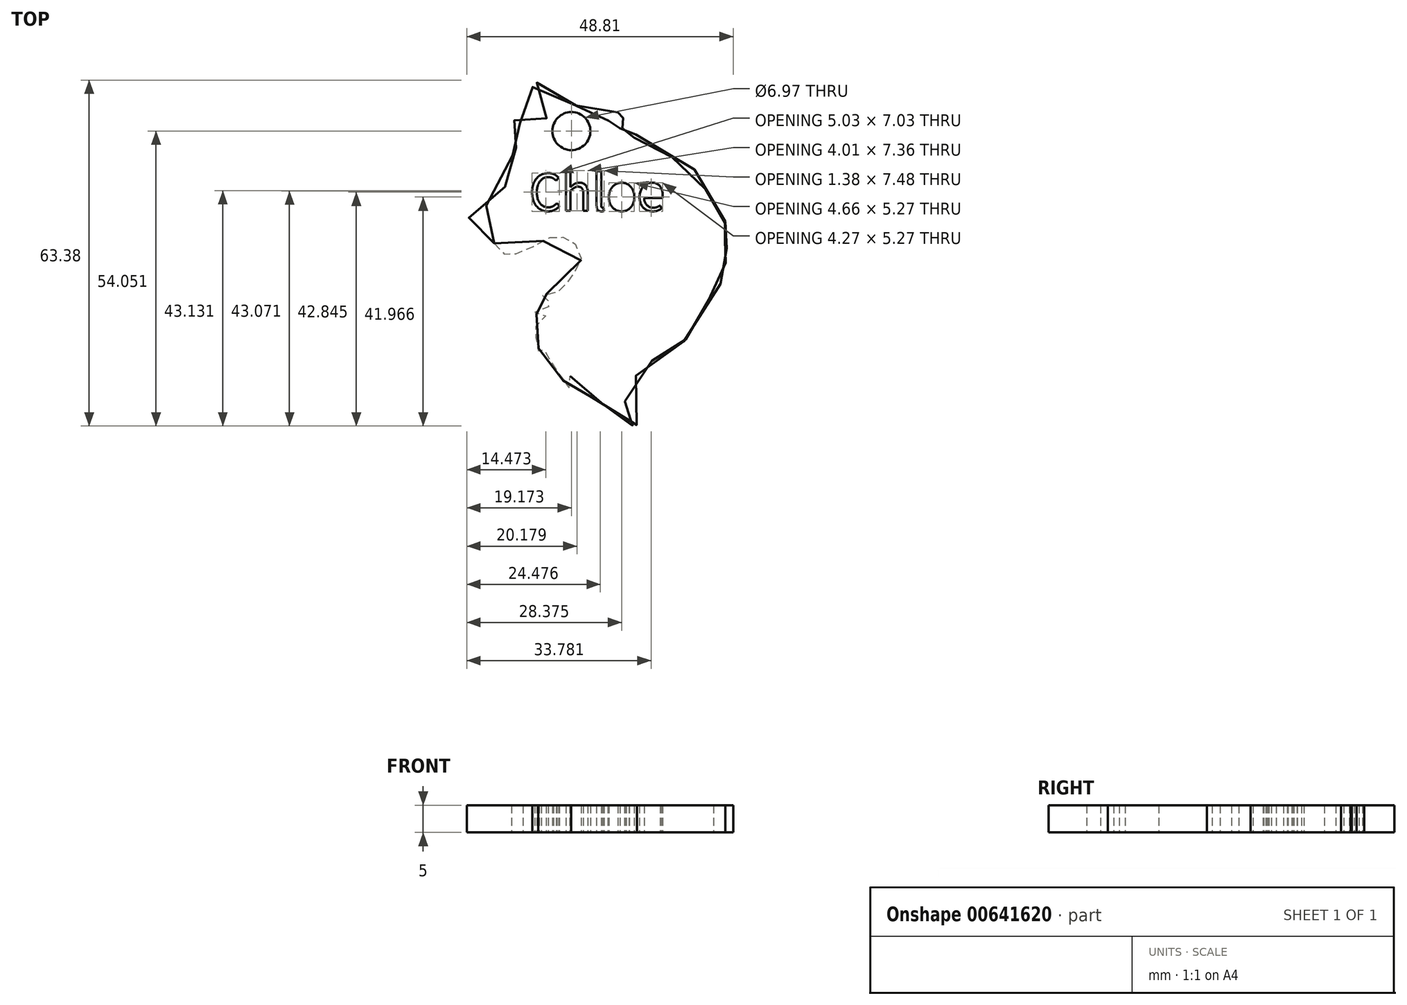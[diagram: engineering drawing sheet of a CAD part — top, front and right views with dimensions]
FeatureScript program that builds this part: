
annotation { "Feature Type Name" : "Feature", "Feature Type Description" : "" }
export const myFeature = defineFeature(function(context is Context, id is Id, definition is map)
    precondition{}
    {
        {
            var Q0;
            Q0=qCreatedBy(makeId("Top.planeOp"),FACE);
            var sketch = newSketch(context, id + "F0", { "sketchPlane" : qUnion([Q0])});
            skFitSpline(sketch, "E0", {"points": [v(-60.78, 16.09) * mm, v(-59.2, 14.31) * mm, v(-58.53, 14.12) * mm, v(-57.08, 14.12) * mm, v(-54.59, 15.03) * mm, v(-51.27, 16.8) * mm, v(-49.26, 17.48) * mm, v(-47.86, 17.1) * mm, v(-46.23, 16.28) * mm, v(-44.93, 14.31) * mm, v(-45.03, 12.4) * mm, v(-46.33, 10.42) * mm, v(-47.2, 9.08) * mm, v(-48.63, 7.88) * mm, v(-49.4, 7.01) * mm, v(-51.75, 6.63) * mm, v(-52.1, 5.81) * mm, v(-50.89, 5.62) * mm, v(-49.93, 5) * mm, v(-52.04, 4.13) * mm, v(-53.34, 3.46) * mm, v(-52.43, 2.88) * mm, v(-51.23, 2.79) * mm, v(-52.95, 1.1) * mm, v(-53.68, -0.91) * mm, v(-52.62, -1.58) * mm, v(-52.67, -3.65) * mm, v(-52.33, -4.42) * mm, v(-51.37, -3.31) * mm, v(-50.46, -5.38) * mm, v(-50.17, -5.9) * mm, v(-48.72, -8.17) * mm, v(-46.9, -10.39) * mm, v(-46.68, -9.75) * mm, v(-46.86, -7.8) * mm, v(-45.86, -9.35) * mm, v(-43.73, -11.57) * mm, v(-38.57, -14.7) * mm, v(-37.48, -15.37) * mm, v(-36.2, -16.33) * mm, v(-35.9, -16.87) * mm, v(-34.99, -17.37) * mm, v(-34.62, -16.92) * mm, v(-35.67, -15.83) * mm, v(-36.2, -14.42) * mm, v(-36.8, -12.84) * mm, v(-36.53, -10.8) * mm, v(-33, -6.13) * mm, v(-31.77, -5.5) * mm, v(-31.45, -6.49) * mm, v(-30.63, -5.72) * mm, v(-26, -1.87) * mm, v(-23.74, 1.04) * mm, v(-22.75, 2.49) * mm, v(-21.52, 5.61) * mm, v(-18.94, 9.1) * mm, v(-18.4, 10.2) * mm, v(-18.45, 12.64) * mm, v(-17.47, 11.67) * mm, v(-16.97, 12.28) * mm, v(-18.2, 15.3) * mm, v(-18.34, 16.35) * mm, v(-19.78, 18.76) * mm, v(-20.53, 19.87) * mm, v(-19.85, 20.09) * mm, v(-18.84, 19.7) * mm, v(-18.34, 19.94) * mm, v(-19.67, 20.95) * mm, v(-20.78, 23.8) * mm, v(-22.15, 26.24) * mm, v(-23.05, 28.69) * mm, v(-26.14, 30.85) * mm, v(-29.35, 32.5) * mm, v(-33.41, 35.1) * mm, v(-34.6, 36.2) * mm, v(-35.28, 35.27) * mm, v(-35.97, 36.35) * mm, v(-36.02, 37.1) * mm, v(-36.07, 37.86) * mm, v(-36.74, 37.96) * mm, v(-37.27, 37.1) * mm, v(-37.48, 36.75) * mm, v(-37.67, 37.3) * mm, v(-36.79, 38.2) * mm, v(-36.7, 38.16) * mm, v(-36.72, 38.8) * mm, v(-36.54, 39.02) * mm, v(-37.85, 38.93) * mm, v(-39.17, 38.07) * mm, v(-39.71, 37.93) * mm, v(-39.82, 38.55) * mm, v(-38.1, 39.97) * mm, v(-38.62, 40.47) * mm, v(-40.3, 39.56) * mm, v(-43.13, 40.5) * mm, v(-48.69, 42.3) * mm, v(-50.75, 43.33) * mm, v(-52.66, 44.93) * mm, v(-53.24, 46) * mm, v(-53.71, 45.7) * mm, v(-53.41, 43.82) * mm, v(-51.02, 38.81) * mm, v(-50.89, 38.3) * mm, v(-52.52, 37.87) * mm, v(-55.98, 38.04) * mm, v(-57.4, 38.64) * mm, v(-57.18, 36.93) * mm, v(-55.51, 35) * mm, v(-56.15, 34.45) * mm, v(-57.22, 32.6) * mm, v(-57.74, 31.41) * mm, v(-58.6, 28.46) * mm, v(-58.9, 25.93) * mm, v(-60.13, 24.14) * mm, v(-63.98, 22.08) * mm, v(-65.78, 19.82) * mm, v(-64.2, 17.68) * mm, v(-61.41, 16.18) * mm, v(-60.78, 16.09) * mm]});
            skText(sketch, "E1", { "text": "Chloe", "fontName": "NotoSansCJKkr-Regular.otf"});
            skCircle(sketch, "E2", {"center": v(-46.6, 36.68) * mm, "radius": 3.49 * mm});
            const initialGuessF0  = {"E1": [-0.05436, 0.02208, 1, 0, 0.00666]};
            skSetInitialGuess(sketch, initialGuessF0);
            skSolve(sketch);
        }
        {
            var Q0;
            Q0=makeQuery(id+"F0.imprint","IMPRINT",FACE,{"disambiguationData":[TD([[makeQuery(id+"F0.imprint","IMPRINT",EDGE,{"derivedFrom":sQuery(id+"F0.wireOp",EDGE,"E0")}),1.0]])]});
            extrude(context, id + "F1", {"entities" : qUnion([Q0]), "depth" : 5 * mm, "offsetDistance" : 25.4 * mm});
        }
        {
            var Q0;
            Q0 = qSketchRegion(id + "F0", true);
            extrude(context, id + "F2", {"entities" : qUnion([Q0]), "operationType" : NewBodyOperationType.ADD, "depth" : 5 * mm, "offsetDistance" : 25 * mm});
        }
    });
